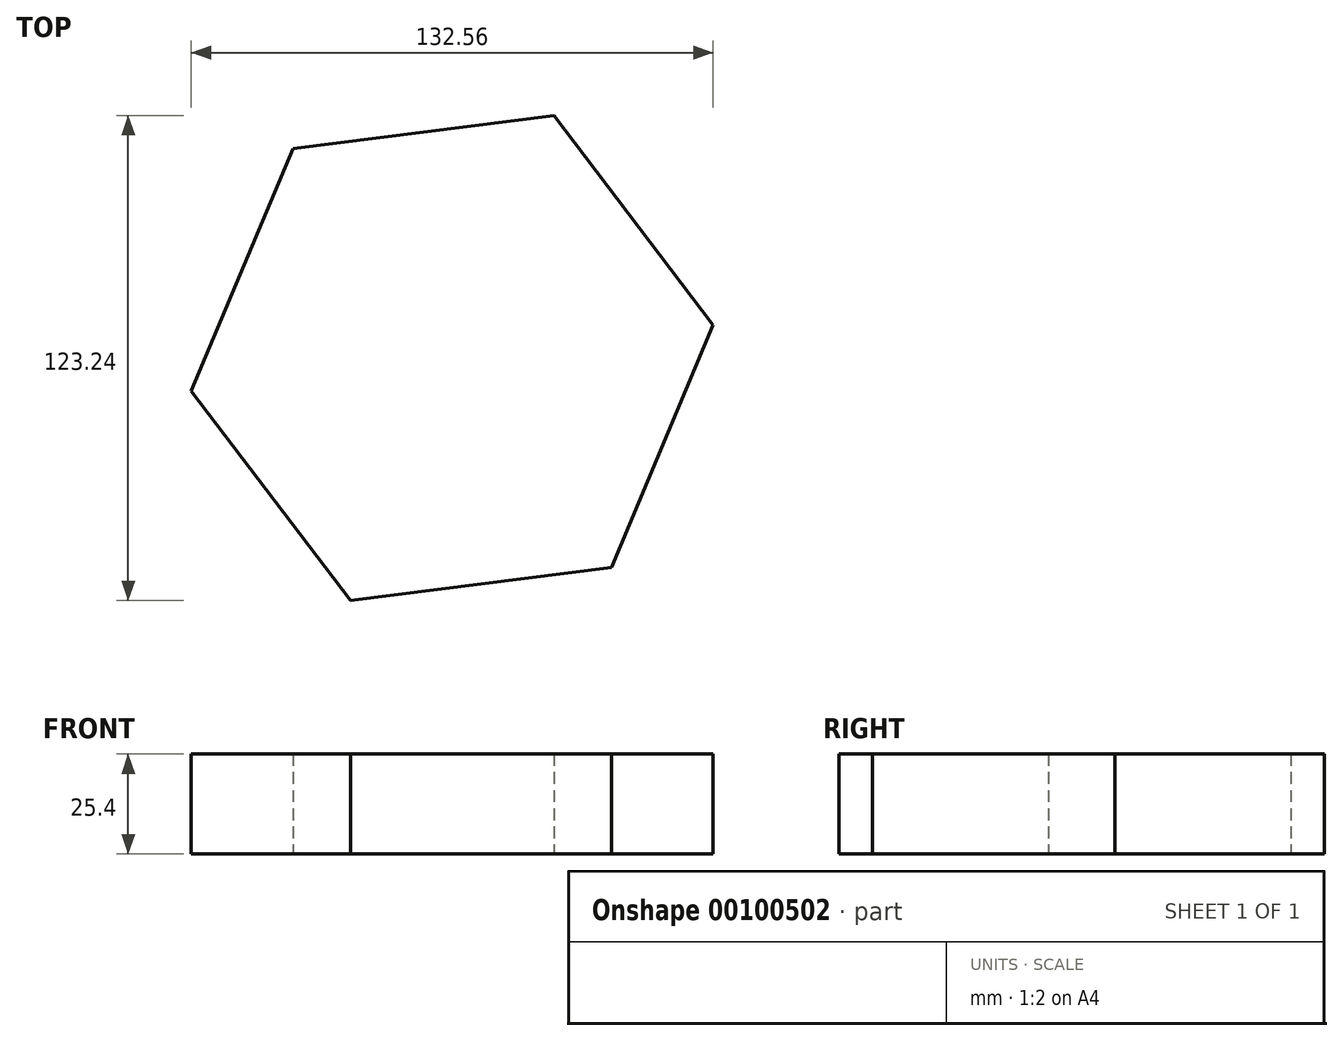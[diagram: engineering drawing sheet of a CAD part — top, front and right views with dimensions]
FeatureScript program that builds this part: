
annotation { "Feature Type Name" : "Feature", "Feature Type Description" : "" }
export const myFeature = defineFeature(function(context is Context, id is Id, definition is map)
    precondition{}
    {
        {
            var Q0;
            Q0=qCreatedBy(makeId("Top.planeOp"),FACE);
            var sketch = newSketch(context, id + "F0", { "sketchPlane" : qUnion([Q0])});
            skCircle(sketch, "E0.cCircle", {"center": v(0, 0) * mm, "radius": 57.86 * mm, "construction": true});
            skLineSegment(sketch, "E0.0", {"start": v(-40.44, 53.19) * mm, "end": v(25.84, 61.62) * mm});
            skLineSegment(sketch, "E0.1", {"start": v(25.84, 61.62) * mm, "end": v(66.28, 8.43) * mm});
            skLineSegment(sketch, "E0.2", {"start": v(66.28, 8.43) * mm, "end": v(40.44, -53.19) * mm});
            skLineSegment(sketch, "E0.3", {"start": v(40.44, -53.19) * mm, "end": v(-25.84, -61.62) * mm});
            skLineSegment(sketch, "E0.4", {"start": v(-25.84, -61.62) * mm, "end": v(-66.28, -8.43) * mm});
            skLineSegment(sketch, "E0.5", {"start": v(-66.28, -8.43) * mm, "end": v(-40.44, 53.19) * mm});
            skPoint(sketch, "E0.0.midPoint", {"position": v(-7.3, 57.4) * mm});
            skSolve(sketch);
        }
        {
            var Q0;
            Q0 = qSketchRegion(id + "F0", true);
            extrude(context, id + "F1", {"entities" : qUnion([Q0]), "depth" : 25.4 * mm});
        }
        {
            var Q0;
            Q0=makeQuery(id+"F1.opExtrude","SWEPT_BODY",BODY,{"disambiguationData":[OSD([sQuery(id+"F0.wireOp",EDGE,"E0.0"),sQuery(id+"F0.wireOp",EDGE,"E0.1"),sQuery(id+"F0.wireOp",EDGE,"E0.2"),sQuery(id+"F0.wireOp",EDGE,"E0.3"),sQuery(id+"F0.wireOp",EDGE,"E0.4"),sQuery(id+"F0.wireOp",EDGE,"E0.5")])]});
            transform(context, id + "F2", {"entities" : qUnion([Q0]), "transformType" : TransformType.TRANSLATION_3D, "dx" : 0 * mm, "dy" : 0 * mm, "dz" : 0 * mm, "makeCopy" : true});
        }
        {
            var Q0;
            Q0=makeQuery(id+"F2.opPattern","COPY",BODY,{"derivedFrom":makeQuery(id+"F1.opExtrude","SWEPT_BODY",BODY,{"disambiguationData":[OSD([sQuery(id+"F0.wireOp",EDGE,"E0.0"),sQuery(id+"F0.wireOp",EDGE,"E0.1"),sQuery(id+"F0.wireOp",EDGE,"E0.2"),sQuery(id+"F0.wireOp",EDGE,"E0.3"),sQuery(id+"F0.wireOp",EDGE,"E0.4"),sQuery(id+"F0.wireOp",EDGE,"E0.5")])]}),"instanceName":"1"});
            transform(context, id + "F3", {"entities" : qUnion([Q0]), "transformType" : TransformType.TRANSLATION_3D, "dx" : 0 * mm, "dy" : 0 * mm, "dz" : 0 * mm, "makeCopy" : true});
        }
    });
